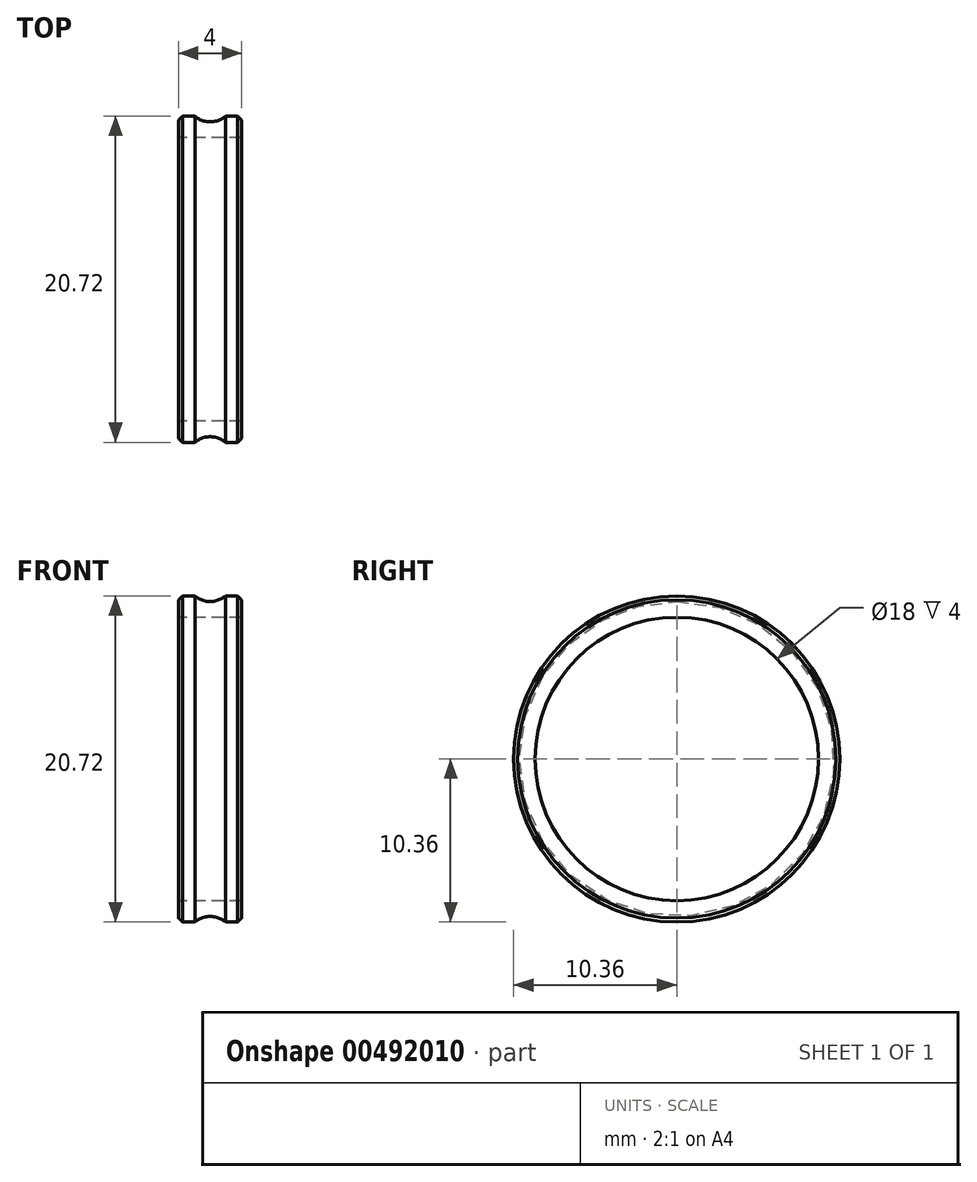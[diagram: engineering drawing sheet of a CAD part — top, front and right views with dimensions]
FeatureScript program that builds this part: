
annotation { "Feature Type Name" : "Feature", "Feature Type Description" : "" }
export const myFeature = defineFeature(function(context is Context, id is Id, definition is map)
    precondition{}
    {
        {
            var Q0;
            Q0=qCreatedBy(makeId("Front.planeOp"),FACE);
            var sketch = newSketch(context, id + "F0", { "sketchPlane" : qUnion([Q0])});
            skArc(sketch, "E0", {"start": v(0, 10) * mm, "mid": v(0.52, 10.1) * mm, "end": v(0.97, 10.36) * mm});
            skLineSegment(sketch, "E1", {"start": v(0.97, 10.36) * mm, "end": v(2, 10.36) * mm});
            skLineSegment(sketch, "E2", {"start": v(2, 10.36) * mm, "end": v(2, 9) * mm});
            skLineSegment(sketch, "E3", {"start": v(2, 9) * mm, "end": v(0, 9) * mm});
            skLineSegment(sketch, "E4", {"start": v(0, 9) * mm, "end": v(0, 10) * mm, "construction": true});
            skLineSegment(sketch, "E5.MirrorCS", {"start": v(-0.97, 10.36) * mm, "end": v(-2, 10.36) * mm});
            skArc(sketch, "E6.MirrorCS", {"start": v(0, 10) * mm, "mid": v(-0.52, 10.1) * mm, "end": v(-0.97, 10.36) * mm});
            skLineSegment(sketch, "E7.MirrorCS", {"start": v(-2, 9) * mm, "end": v(0, 9) * mm});
            skLineSegment(sketch, "E8.MirrorCS", {"start": v(-2, 10.36) * mm, "end": v(-2, 9) * mm});
            skLineSegment(sketch, "E9", {"start": v(-3.7, 0) * mm, "end": v(4.46, 0) * mm, "construction": true});
            skSolve(sketch);
        }
        {
            var Q0;
            Q0=makeQuery(id+"F0.imprint","IMPRINT",FACE,{"disambiguationData":[TD([[makeQuery(id+"F0.imprint","IMPRINT",EDGE,{"derivedFrom":sQuery(id+"F0.wireOp",EDGE,"E0")}),-1.0]])]});
            var Q1;
            Q1=sQuery(id+"F0.wireOp",EDGE,"E9");
            revolve(context, id + "F1", {"entities" : qUnion([Q0]), "axis" : qUnion([Q1]), "revolveType" : RevolveType.FULL});
        }
        {
            var Q0;
            Q0=makeQuery(id+"F1.opRevolve","SWEPT_EDGE",EDGE,{"disambiguationData":[OSD([sQuery(id+"F0.wireOp",EDGE,"E1"),sQuery(id+"F0.wireOp",EDGE,"E2")])]});
            var Q1;
            Q1=makeQuery(id+"F1.opRevolve","SWEPT_EDGE",EDGE,{"disambiguationData":[OSD([sQuery(id+"F0.wireOp",EDGE,"E5.MirrorCS"),sQuery(id+"F0.wireOp",EDGE,"E8.MirrorCS")])]});
            chamfer(context, id + "F2", {"entities" : qUnion([Q0, Q1]), "width" : .25 * mm, "tangentPropagation" : true});
        }
    });
